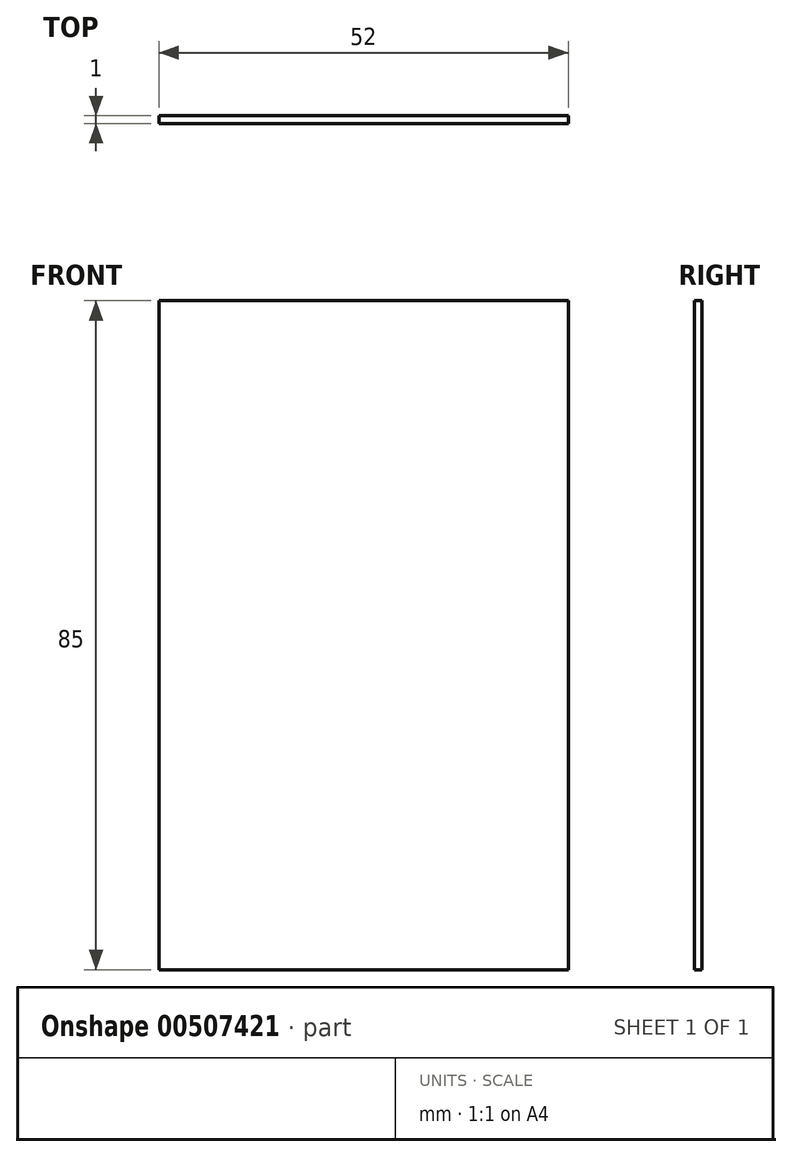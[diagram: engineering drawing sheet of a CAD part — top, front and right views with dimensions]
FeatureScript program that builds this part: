
annotation { "Feature Type Name" : "Feature", "Feature Type Description" : "" }
export const myFeature = defineFeature(function(context is Context, id is Id, definition is map)
    precondition{}
    {
        {
            var Q0;
            Q0=qCreatedBy(makeId("Front.planeOp"),FACE);
            var sketch = newSketch(context, id + "F0", { "sketchPlane" : qUnion([Q0])});
            skLineSegment(sketch, "E0.bottom", {"start": v(-52, 0) * mm, "end": v(0, 0) * mm});
            skLineSegment(sketch, "E0.top", {"start": v(-52, 85) * mm, "end": v(0, 85) * mm});
            skLineSegment(sketch, "E0.left", {"start": v(-52, 0) * mm, "end": v(-52, 85) * mm});
            skLineSegment(sketch, "E0.right", {"start": v(0, 0) * mm, "end": v(0, 85) * mm});
            skLineSegment(sketch, "E1", {"start": v(-26, 85) * mm, "end": v(-26, 0) * mm, "construction": true});
            skSolve(sketch);
        }
        {
            var Q0;
            Q0=makeQuery(id+"F0.imprint","IMPRINT",FACE,{"disambiguationData":[TD([[makeQuery(id+"F0.imprint","IMPRINT",EDGE,{"derivedFrom":sQuery(id+"F0.wireOp",EDGE,"E0.bottom")}),1.0]])]});
            extrude(context, id + "F1", {"entities" : qUnion([Q0]), "depth" : 1 * mm});
        }
    });
